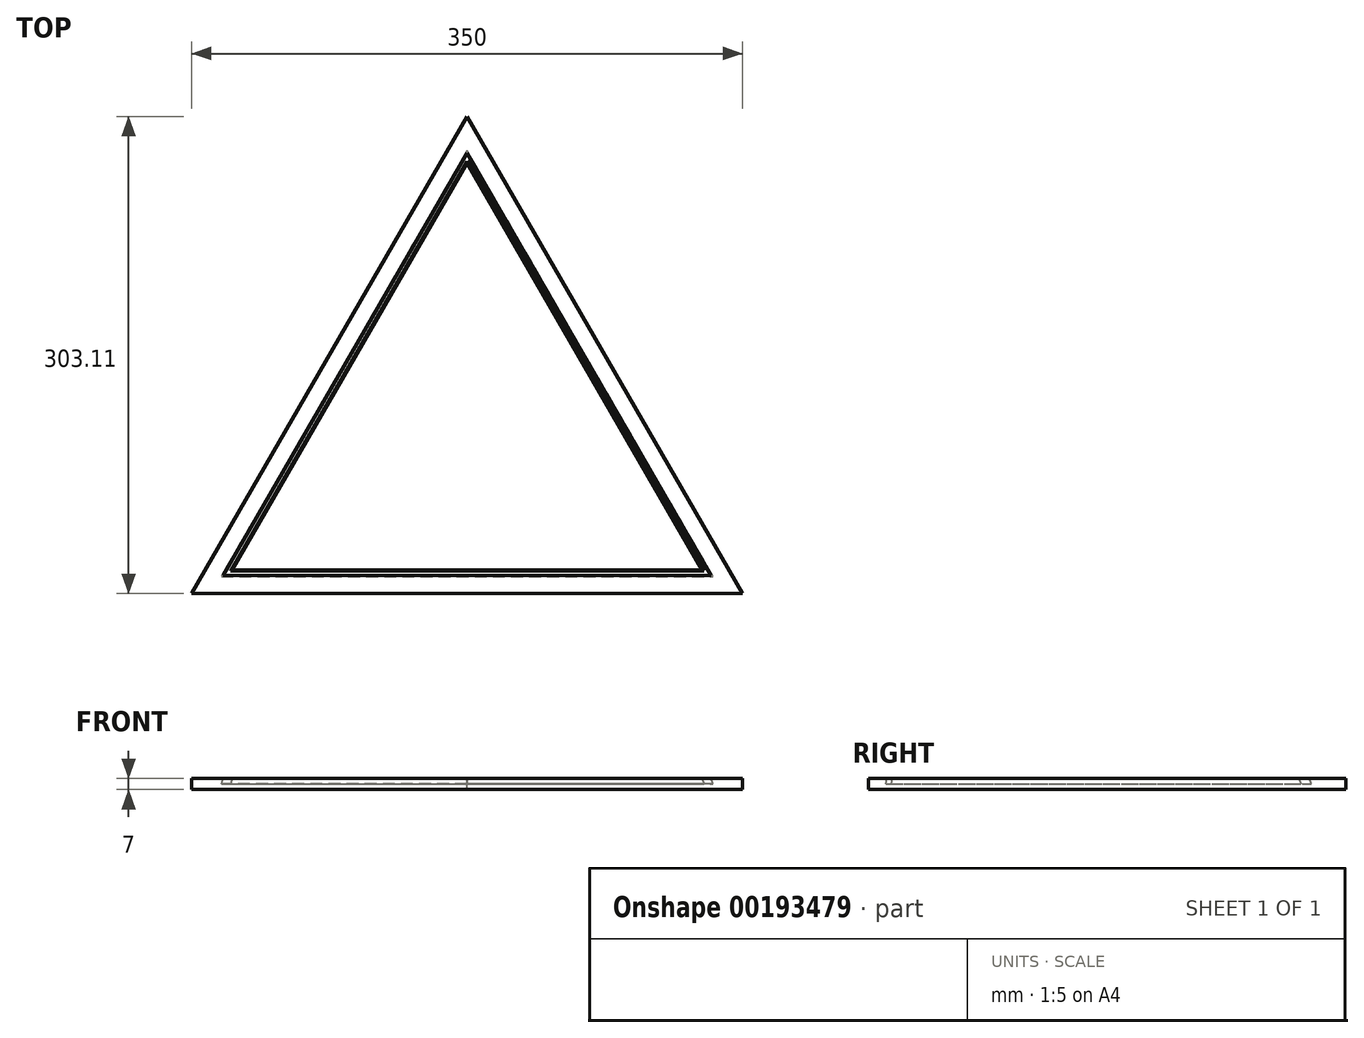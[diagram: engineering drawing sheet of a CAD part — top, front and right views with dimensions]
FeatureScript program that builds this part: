
annotation { "Feature Type Name" : "Feature", "Feature Type Description" : "" }
export const myFeature = defineFeature(function(context is Context, id is Id, definition is map)
    precondition{}
    {
        {
            var Q0;
            Q0=qCreatedBy(makeId("Top.planeOp"),FACE);
            var sketch = newSketch(context, id + "F0", { "sketchPlane" : qUnion([Q0])});
            skLineSegment(sketch, "E0", {"start": v(0, 202.07) * mm, "end": v(-175, -101.04) * mm});
            skLineSegment(sketch, "E1", {"start": v(-175, -101.04) * mm, "end": v(0, 202.07) * mm});
            skLineSegment(sketch, "E2", {"start": v(0, 0) * mm, "end": v(0, 202.07) * mm, "construction": true});
            skLineSegment(sketch, "E3", {"start": v(0, 0) * mm, "end": v(-175, -101.04) * mm, "construction": true});
            skLineSegment(sketch, "E4.MirrorCS", {"start": v(0, 202.07) * mm, "end": v(175, -101.04) * mm});
            skLineSegment(sketch, "E5.MirrorCS", {"start": v(0, 0) * mm, "end": v(175, -101.04) * mm, "construction": true});
            skLineSegment(sketch, "E6", {"start": v(-175, -101.04) * mm, "end": v(175, -101.04) * mm});
            skLineSegment(sketch, "E7.0", {"start": v(0, 172.27) * mm, "end": v(149.19, -86.13) * mm, "construction": true});
            skLineSegment(sketch, "E7.1", {"start": v(-149.19, -86.13) * mm, "end": v(0, 172.27) * mm, "construction": true});
            skLineSegment(sketch, "E7.2", {"start": v(-149.19, -86.13) * mm, "end": v(149.19, -86.13) * mm, "construction": true});
            skSolve(sketch);
        }
        {
            var Q0;
            Q0 = qSketchRegion(id + "F0", true);
            extrude(context, id + "F4", {"entities" : qUnion([Q0]), "oppositeDirection" : true, "depth" : 7 * mm});
        }
        {
            var Q0;
            Q0=qCreatedBy(makeId("Right.planeOp"),FACE);
            var sketch = newSketch(context, id + "F1", { "sketchPlane" : qUnion([Q0])});
            skPoint(sketch, "E8.0", {"position": v(-86.13, 0) * mm});
            skLineSegment(sketch, "E9", {"start": v(-86.13, 0) * mm, "end": v(-89.44, 0) * mm});
            skLineSegment(sketch, "E10", {"start": v(-89.44, 0) * mm, "end": v(-90.12, -3.5) * mm});
            skLineSegment(sketch, "E11", {"start": v(-90.12, -3.5) * mm, "end": v(-86.81, -3.5) * mm});
            skLineSegment(sketch, "E12", {"start": v(-86.81, -3.5) * mm, "end": v(-86.13, 0) * mm});
            skSolve(sketch);
        }
        {
            var Q0;
            Q0=qCreatedBy(makeId("Top.planeOp"),FACE);
            var sketch = newSketch(context, id + "F2", { "sketchPlane" : qUnion([Q0])});
            skLineSegment(sketch, "E13.0", {"start": v(-149.19, -86.13) * mm, "end": v(149.19, -86.13) * mm});
            skLineSegment(sketch, "E13.1", {"start": v(-149.19, -86.13) * mm, "end": v(0, 172.27) * mm});
            skLineSegment(sketch, "E13.2", {"start": v(0, 172.27) * mm, "end": v(149.19, -86.13) * mm});
            skSolve(sketch);
        }
        {
            var Q0;
            Q0 = qSketchRegion(id + "F1", true);
            var Q1;
            Q1 = qConstructionFilter(qBodyType(qCreatedBy(id + "F2" ,EDGE), BodyType.WIRE), ConstructionObject.NO);
            sweep(context, id + "F3", {"operationType" : NewBodyOperationType.REMOVE, "profiles" : qUnion([Q0]), "path" : qUnion([Q1])});
        }
    });
